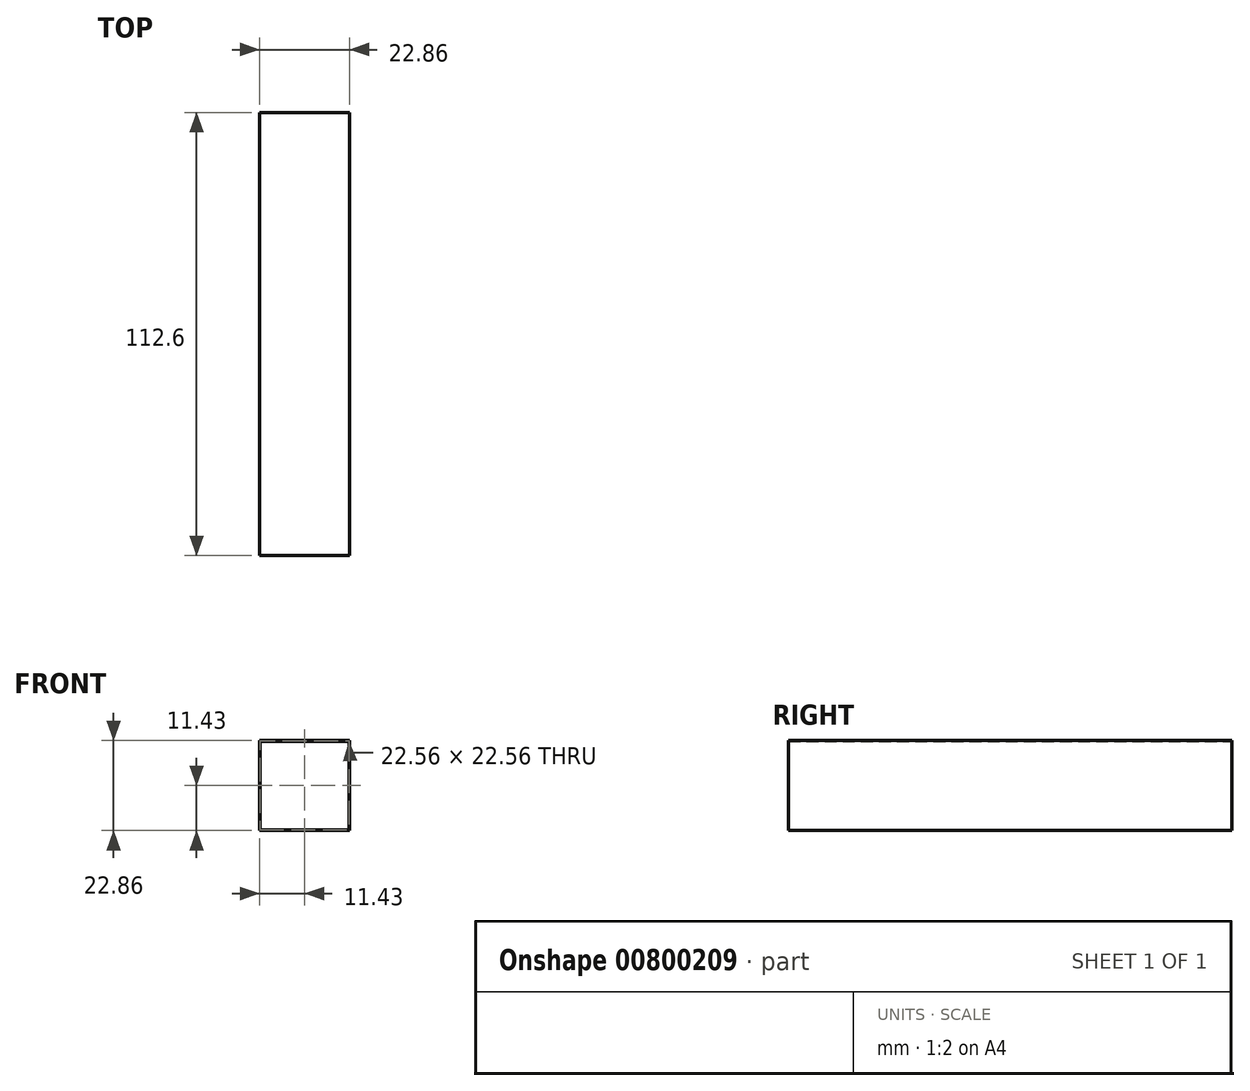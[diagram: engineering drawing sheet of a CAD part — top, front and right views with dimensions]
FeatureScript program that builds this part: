
annotation { "Feature Type Name" : "Feature", "Feature Type Description" : "" }
export const myFeature = defineFeature(function(context is Context, id is Id, definition is map)
    precondition{}
    {
        {
            var Q0;
            Q0=qCreatedBy(makeId("Front.planeOp"),FACE);
            var sketch = newSketch(context, id + "F0", { "sketchPlane" : qUnion([Q0])});
            skLineSegment(sketch, "E0.bottom", {"start": v(-11.43, 11.43) * mm, "end": v(11.43, 11.43) * mm});
            skLineSegment(sketch, "E0.top", {"start": v(-11.43, -11.43) * mm, "end": v(11.43, -11.43) * mm});
            skLineSegment(sketch, "E0.left", {"start": v(-11.43, 11.43) * mm, "end": v(-11.43, -11.43) * mm});
            skLineSegment(sketch, "E0.right", {"start": v(11.43, 11.43) * mm, "end": v(11.43, -11.43) * mm});
            skPoint(sketch, "E0.middle", {"position": v(0, 0) * mm});
            skLineSegment(sketch, "E1.bottom", {"start": v(-11.28, 11.28) * mm, "end": v(11.28, 11.28) * mm});
            skLineSegment(sketch, "E1.top", {"start": v(-11.28, -11.28) * mm, "end": v(11.28, -11.28) * mm});
            skLineSegment(sketch, "E1.left", {"start": v(-11.28, 11.28) * mm, "end": v(-11.28, -11.28) * mm});
            skLineSegment(sketch, "E1.right", {"start": v(11.28, 11.28) * mm, "end": v(11.28, -11.28) * mm});
            skSolve(sketch);
        }
        {
            var Q0;
            Q0=qSketchRegion(id+"F0",true);
            extrude(context, id + "F1", {"entities" : qUnion([Q0]), "depth" : 87.6 * mm, "offsetDistance" : 25 * mm, "hasSecondDirection" : true, "secondDirectionOppositeDirection" : true, "secondDirectionDepth" : 25 * mm});
        }
    });
